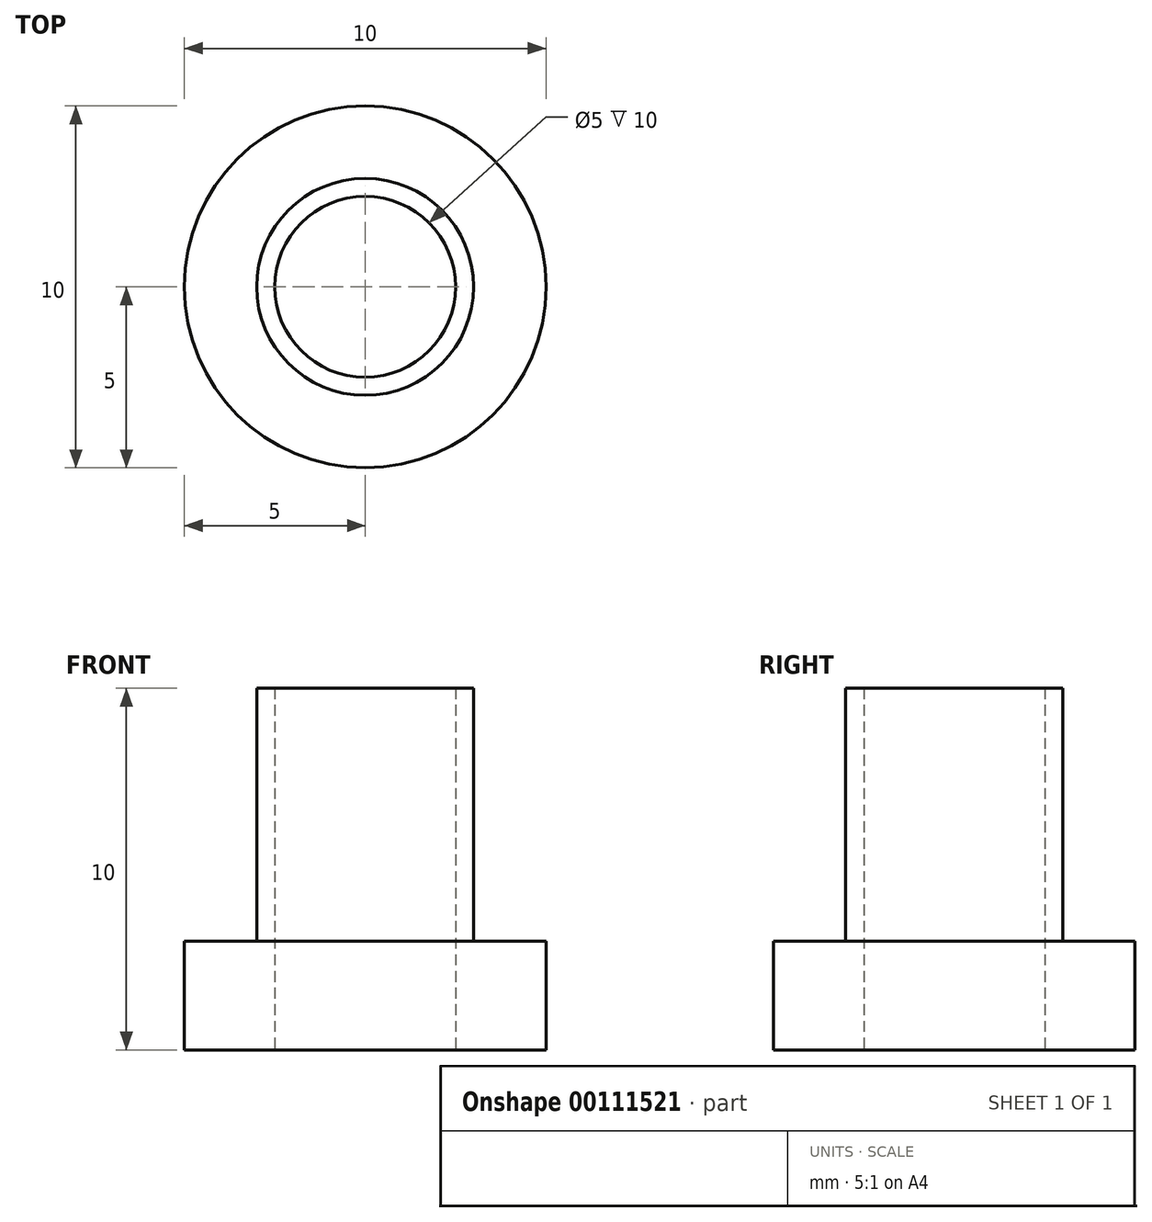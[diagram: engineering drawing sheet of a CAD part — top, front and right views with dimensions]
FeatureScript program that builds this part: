
annotation { "Feature Type Name" : "Feature", "Feature Type Description" : "" }
export const myFeature = defineFeature(function(context is Context, id is Id, definition is map)
    precondition{}
    {
        {
            var Q0;
            Q0=qCreatedBy(makeId("Top.planeOp"),FACE);
            var sketch = newSketch(context, id + "F0", { "sketchPlane" : qUnion([Q0])});
            skCircle(sketch, "E0", {"center": v(0, 0) * mm, "radius": 5 * mm});
            skCircle(sketch, "E1", {"center": v(0, 0) * mm, "radius": 3 * mm});
            skLineSegment(sketch, "E2", {"start": v(0, 0) * mm, "end": v(0, 5) * mm});
            skLineSegment(sketch, "E3", {"start": v(0, 5) * mm, "end": v(0, 0) * mm});
            skLineSegment(sketch, "E4", {"start": v(0, 0) * mm, "end": v(5, 0) * mm});
            skLineSegment(sketch, "E5", {"start": v(0, 0) * mm, "end": v(-5, 0) * mm});
            skLineSegment(sketch, "E6", {"start": v(0, 0) * mm, "end": v(0, -5) * mm});
            skCircle(sketch, "E7", {"center": v(0, 0) * mm, "radius": 2.5 * mm});
            skSolve(sketch);
        }
        {
            var Q0;
            {var subQ0=sQuery(id+"F0.wireOp",EDGE,"E3");var subQ1=sQuery(id+"F0.wireOp",EDGE,"E1");var subQ2=makeQuery(id+"F0.imprint","INTERSECT",VERTEX,{"derivedFrom":[subQ1,subQ0]});Q0=makeQuery(id+"F0.imprint","IMPRINT",FACE,{"disambiguationData":[TD([[makeQuery(id+"F0.imprint","IMPRINT",EDGE,{"disambiguationData":[TD([[subQ2,-1.0]])],"derivedFrom":subQ1}),1.0]])]});}
            var Q1;
            {var subQ0=sQuery(id+"F0.wireOp",EDGE,"E5");var subQ1=sQuery(id+"F0.wireOp",EDGE,"E1");var subQ2=makeQuery(id+"F0.imprint","INTERSECT",VERTEX,{"derivedFrom":[subQ1,subQ0]});Q1=makeQuery(id+"F0.imprint","IMPRINT",FACE,{"disambiguationData":[TD([[makeQuery(id+"F0.imprint","IMPRINT",EDGE,{"disambiguationData":[TD([[subQ2,-1.0]])],"derivedFrom":subQ1}),1.0]])]});}
            var Q2;
            {var subQ0=sQuery(id+"F0.wireOp",EDGE,"E4");var subQ1=sQuery(id+"F0.wireOp",EDGE,"E1");var subQ2=makeQuery(id+"F0.imprint","INTERSECT",VERTEX,{"derivedFrom":[subQ1,subQ0]});Q2=makeQuery(id+"F0.imprint","IMPRINT",FACE,{"disambiguationData":[TD([[makeQuery(id+"F0.imprint","IMPRINT",EDGE,{"disambiguationData":[TD([[subQ2,1.0]])],"derivedFrom":subQ1}),1.0]])]});}
            var Q3;
            {var subQ0=sQuery(id+"F0.wireOp",EDGE,"E3");var subQ1=sQuery(id+"F0.wireOp",EDGE,"E1");var subQ2=makeQuery(id+"F0.imprint","INTERSECT",VERTEX,{"derivedFrom":[subQ1,subQ0]});Q3=makeQuery(id+"F0.imprint","IMPRINT",FACE,{"disambiguationData":[TD([[makeQuery(id+"F0.imprint","IMPRINT",EDGE,{"disambiguationData":[TD([[subQ2,1.0]])],"derivedFrom":subQ1}),1.0]])]});}
            extrude(context, id + "F1", {"entities" : qUnion([Q0, Q1, Q2, Q3]), "depth" : 10 * mm});
        }
        {
            var Q0;
            {var subQ0=sQuery(id+"F0.wireOp",EDGE,"E3");var subQ1=sQuery(id+"F0.wireOp",EDGE,"E0");var subQ2=makeQuery(id+"F0.imprint","INTERSECT",VERTEX,{"derivedFrom":[subQ1,subQ0]});Q0=makeQuery(id+"F0.imprint","IMPRINT",FACE,{"disambiguationData":[TD([[makeQuery(id+"F0.imprint","IMPRINT",EDGE,{"disambiguationData":[TD([[subQ2,-1.0]])],"derivedFrom":subQ1}),1.0]])]});}
            var Q1;
            {var subQ0=sQuery(id+"F0.wireOp",EDGE,"E4");var subQ1=sQuery(id+"F0.wireOp",EDGE,"E0");var subQ2=makeQuery(id+"F0.imprint","INTERSECT",VERTEX,{"derivedFrom":[subQ1,subQ0]});Q1=makeQuery(id+"F0.imprint","IMPRINT",FACE,{"disambiguationData":[TD([[makeQuery(id+"F0.imprint","IMPRINT",EDGE,{"disambiguationData":[TD([[subQ2,1.0]])],"derivedFrom":subQ1}),1.0]])]});}
            var Q2;
            {var subQ0=sQuery(id+"F0.wireOp",EDGE,"E5");var subQ1=sQuery(id+"F0.wireOp",EDGE,"E0");var subQ2=makeQuery(id+"F0.imprint","INTERSECT",VERTEX,{"derivedFrom":[subQ1,subQ0]});Q2=makeQuery(id+"F0.imprint","IMPRINT",FACE,{"disambiguationData":[TD([[makeQuery(id+"F0.imprint","IMPRINT",EDGE,{"disambiguationData":[TD([[subQ2,-1.0]])],"derivedFrom":subQ1}),1.0]])]});}
            var Q3;
            {var subQ0=sQuery(id+"F0.wireOp",EDGE,"E3");var subQ1=sQuery(id+"F0.wireOp",EDGE,"E1");var subQ2=makeQuery(id+"F0.imprint","INTERSECT",VERTEX,{"derivedFrom":[subQ1,subQ0]});Q3=makeQuery(id+"F0.imprint","IMPRINT",FACE,{"disambiguationData":[TD([[makeQuery(id+"F0.imprint","IMPRINT",EDGE,{"disambiguationData":[TD([[subQ2,-1.0]])],"derivedFrom":subQ1}),-1.0]])]});}
            var Q4;
            {var subQ0=sQuery(id+"F0.wireOp",EDGE,"E5");var subQ1=sQuery(id+"F0.wireOp",EDGE,"E1");var subQ2=makeQuery(id+"F0.imprint","INTERSECT",VERTEX,{"derivedFrom":[subQ1,subQ0]});Q4=makeQuery(id+"F0.imprint","IMPRINT",FACE,{"disambiguationData":[TD([[makeQuery(id+"F0.imprint","IMPRINT",EDGE,{"disambiguationData":[TD([[subQ2,-1.0]])],"derivedFrom":subQ1}),-1.0]])]});}
            var Q5;
            {var subQ0=sQuery(id+"F0.wireOp",EDGE,"E4");var subQ1=sQuery(id+"F0.wireOp",EDGE,"E1");var subQ2=makeQuery(id+"F0.imprint","INTERSECT",VERTEX,{"derivedFrom":[subQ1,subQ0]});Q5=makeQuery(id+"F0.imprint","IMPRINT",FACE,{"disambiguationData":[TD([[makeQuery(id+"F0.imprint","IMPRINT",EDGE,{"disambiguationData":[TD([[subQ2,1.0]])],"derivedFrom":subQ1}),-1.0]])]});}
            var Q6;
            {var subQ0=sQuery(id+"F0.wireOp",EDGE,"E3");var subQ1=sQuery(id+"F0.wireOp",EDGE,"E0");var subQ2=makeQuery(id+"F0.imprint","INTERSECT",VERTEX,{"derivedFrom":[subQ1,subQ0]});Q6=makeQuery(id+"F0.imprint","IMPRINT",FACE,{"disambiguationData":[TD([[makeQuery(id+"F0.imprint","IMPRINT",EDGE,{"disambiguationData":[TD([[subQ2,1.0]])],"derivedFrom":subQ1}),1.0]])]});}
            extrude(context, id + "F2", {"entities" : qUnion([Q0, Q1, Q2, Q3, Q4, Q5, Q6]), "operationType" : NewBodyOperationType.ADD, "depth" : 3 * mm});
        }
    });
